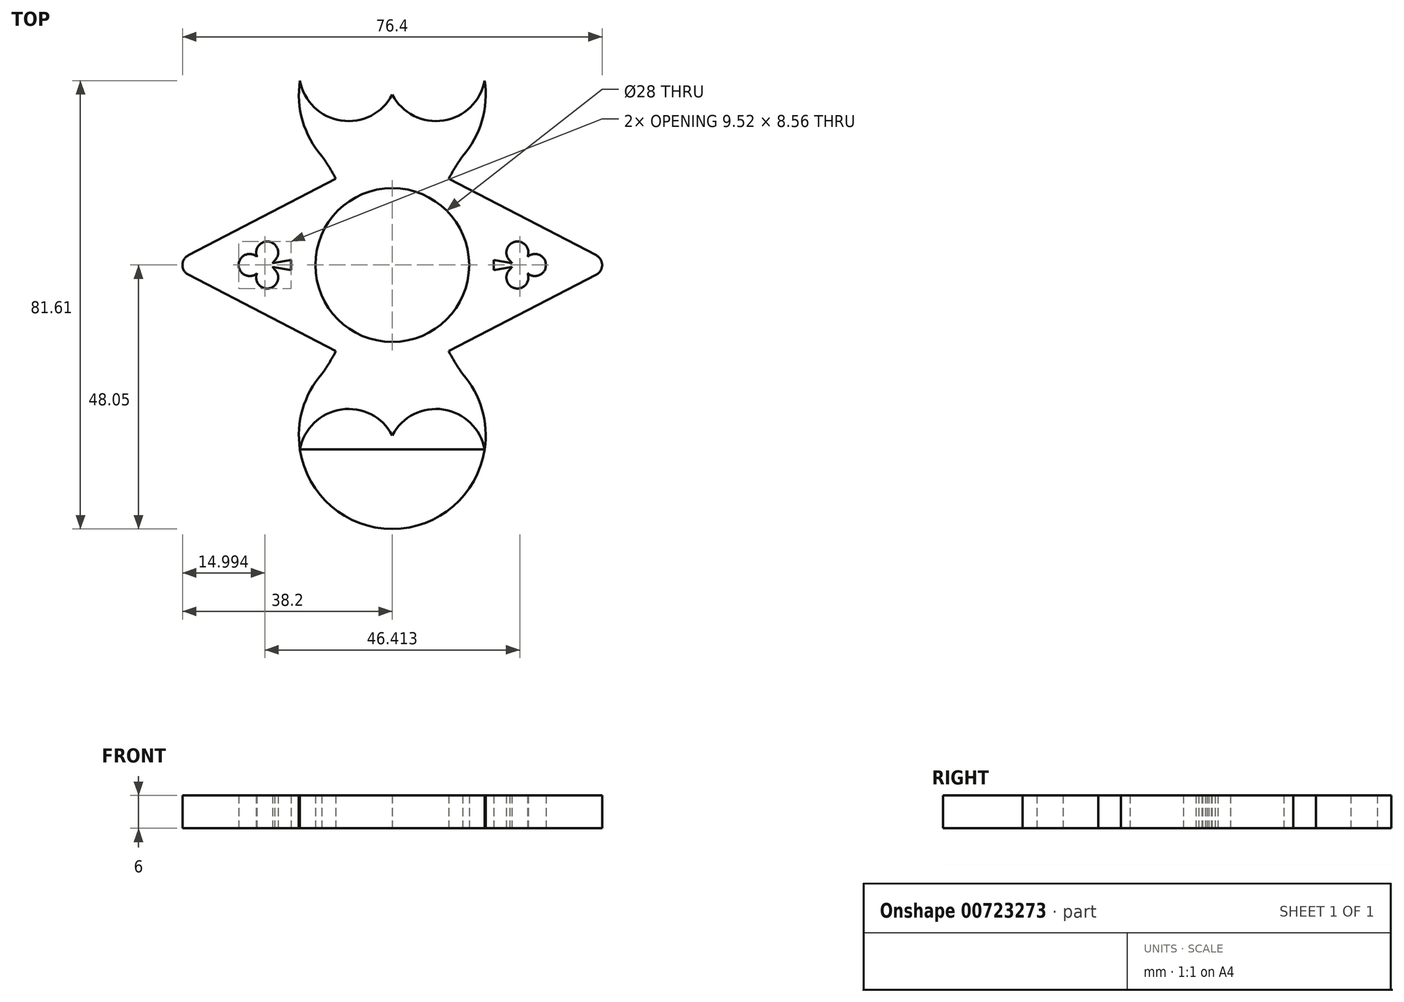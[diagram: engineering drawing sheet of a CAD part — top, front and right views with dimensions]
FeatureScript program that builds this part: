
annotation { "Feature Type Name" : "Feature", "Feature Type Description" : "" }
export const myFeature = defineFeature(function(context is Context, id is Id, definition is map)
    precondition{}
    {
        {
            var Q0;
            Q0=qCreatedBy(makeId("Top.planeOp"),FACE);
            var sketch = newSketch(context, id + "F0", { "sketchPlane" : qUnion([Q0])});
            skCircle(sketch, "E0", {"center": v(0, 0) * mm, "radius": 11 * mm});
            skCircle(sketch, "E1", {"center": v(0, 0) * mm, "radius": 14 * mm});
            skArc(sketch, "E2", {"start": v(-16.8, 33.56) * mm, "mid": v(0, 14) * mm, "end": v(16.8, 33.56) * mm});
            skArc(sketch, "E3", {"start": v(-16.8, 33.56) * mm, "mid": v(-9.31, 26.3) * mm, "end": v(0, 31) * mm});
            skArc(sketch, "E4", {"start": v(0, 31) * mm, "mid": v(9.31, 26.3) * mm, "end": v(16.8, 33.56) * mm});
            skArc(sketch, "E5.MirrorCS", {"start": v(-16.8, -33.56) * mm, "mid": v(-9.31, -26.3) * mm, "end": v(0, -31) * mm});
            skArc(sketch, "E6.MirrorCS", {"start": v(-16.8, -33.56) * mm, "mid": v(0, -14) * mm, "end": v(16.8, -33.56) * mm});
            skArc(sketch, "E7.MirrorCS", {"start": v(0, -31) * mm, "mid": v(9.31, -26.3) * mm, "end": v(16.8, -33.56) * mm});
            skArc(sketch, "E8", {"start": v(-12.8, -19.82) * mm, "mid": v(-11.47, -17.8) * mm, "end": v(-10.27, -15.68) * mm});
            skArc(sketch, "E9.trimOffspring", {"start": v(-10.27, 15.68) * mm, "mid": v(-11.47, 17.8) * mm, "end": v(-12.8, 19.82) * mm});
            skLineSegment(sketch, "E10", {"start": v(-10.27, 15.68) * mm, "end": v(-40.54, 0) * mm});
            skLineSegment(sketch, "E11", {"start": v(-10.27, -15.68) * mm, "end": v(-40.54, 0) * mm});
            skLineSegment(sketch, "E12.MirrorCS", {"start": v(-10.27, 15.68) * mm, "end": v(-37.12, 1.78) * mm});
            skLineSegment(sketch, "E13.MirrorCS", {"start": v(-10.27, -15.68) * mm, "end": v(-37.12, -1.78) * mm});
            skArc(sketch, "E14.MirrorCS", {"start": v(-10.27, -15.68) * mm, "mid": v(-11.47, -17.8) * mm, "end": v(-12.8, -19.82) * mm});
            skLineSegment(sketch, "E15.MirrorCS", {"start": v(10.27, 15.68) * mm, "end": v(37.12, 1.78) * mm});
            skLineSegment(sketch, "E16.MirrorCS", {"start": v(10.27, -15.68) * mm, "end": v(40.54, 0) * mm});
            skLineSegment(sketch, "E17.MirrorCS", {"start": v(10.27, -15.68) * mm, "end": v(37.12, -1.78) * mm});
            skLineSegment(sketch, "E18.MirrorCS", {"start": v(10.27, 15.68) * mm, "end": v(40.54, 0) * mm});
            skArc(sketch, "E19", {"start": v(-24.6, 1.45) * mm, "mid": v(-27.97, 0) * mm, "end": v(-24.6, -1.48) * mm});
            skArc(sketch, "E20", {"start": v(-21.41, 0.81) * mm, "mid": v(-22.39, 4.24) * mm, "end": v(-24.6, 1.45) * mm});
            skArc(sketch, "E21", {"start": v(-24.6, -1.48) * mm, "mid": v(-22.37, -4.24) * mm, "end": v(-21.41, -0.81) * mm});
            skPoint(sketch, "E22.orphan", {"position": v(-24.15, 0.81) * mm});
            skPoint(sketch, "E23.orphan", {"position": v(-24.14, -0.81) * mm});
            skLineSegment(sketch, "E24", {"start": v(-21.77, 0.33) * mm, "end": v(-18.44, 0.92) * mm});
            skLineSegment(sketch, "E25", {"start": v(-21.77, 0) * mm, "end": v(-16.49, 0) * mm, "construction": true});
            skLineSegment(sketch, "E26.MirrorCS", {"start": v(-21.77, -0.33) * mm, "end": v(-18.44, -0.92) * mm});
            skLineSegment(sketch, "E27", {"start": v(-18.44, -0.92) * mm, "end": v(-18.44, 0.92) * mm});
            skFitSpline(sketch, "E28", {"points": [v(-21.41, -0.81) * mm, v(-21.77, -0.33) * mm, v(-21.77, 0) * mm], "startDerivative": vector(-0.8, 0.89) * mm, "endDerivative": vector(0.13, 0.76) * mm});
            skFitSpline(sketch, "E29.MirrorCS", {"points": [v(-21.41, 0.81) * mm, v(-21.77, 0.33) * mm, v(-21.77, 0) * mm], "startDerivative": vector(-0.8, -0.89) * mm, "endDerivative": vector(0.13, -0.76) * mm});
            skFitSpline(sketch, "E30.MirrorCS", {"points": [v(-21.41, 0.81) * mm, v(-21.77, 0.33) * mm, v(-21.77, 0) * mm], "startDerivative": vector(-0.8, -0.89) * mm, "endDerivative": vector(0.13, -0.76) * mm});
            skFitSpline(sketch, "E31.MirrorCS", {"points": [v(-21.41, -0.81) * mm, v(-21.77, -0.33) * mm, v(-21.77, 0) * mm], "startDerivative": vector(-0.8, 0.89) * mm, "endDerivative": vector(0.13, 0.76) * mm});
            skPoint(sketch, "E32.MirrorP", {"position": v(-24.15, -0.81) * mm});
            skArc(sketch, "E33.MirrorCS", {"start": v(-24.6, -1.45) * mm, "mid": v(-27.97, 0) * mm, "end": v(-24.6, 1.48) * mm});
            skArc(sketch, "E34.MirrorCS", {"start": v(-21.41, -0.81) * mm, "mid": v(-22.39, -4.24) * mm, "end": v(-24.6, -1.45) * mm});
            skArc(sketch, "E35.MirrorCS", {"start": v(-24.6, 1.48) * mm, "mid": v(-22.37, 4.24) * mm, "end": v(-21.41, 0.81) * mm});
            skPoint(sketch, "E36.MirrorP", {"position": v(-24.14, 0.81) * mm});
            skLineSegment(sketch, "E37.MirrorCS", {"start": v(-18.44, 0.92) * mm, "end": v(-18.44, -0.92) * mm});
            skArc(sketch, "E38.MirrorCS", {"start": v(10.27, 15.68) * mm, "mid": v(11.47, 17.8) * mm, "end": v(12.8, 19.82) * mm});
            skFitSpline(sketch, "E39.MirrorCS", {"points": [v(21.41, -0.81) * mm, v(21.77, -0.33) * mm, v(21.77, 0) * mm], "startDerivative": vector(0.8, 0.89) * mm, "endDerivative": vector(-0.13, 0.76) * mm});
            skFitSpline(sketch, "E40.MirrorCS", {"points": [v(21.41, 0.81) * mm, v(21.77, 0.33) * mm, v(21.77, 0) * mm], "startDerivative": vector(0.8, -0.89) * mm, "endDerivative": vector(-0.13, -0.76) * mm});
            skPoint(sketch, "E41.MirrorP", {"position": v(24.15, 0.81) * mm});
            skPoint(sketch, "E42.MirrorP", {"position": v(24.15, -0.81) * mm});
            skLineSegment(sketch, "E43.MirrorCS", {"start": v(21.77, -0.33) * mm, "end": v(18.44, -0.92) * mm});
            skLineSegment(sketch, "E44.MirrorCS", {"start": v(21.77, 0.33) * mm, "end": v(18.44, 0.92) * mm});
            skLineSegment(sketch, "E45.MirrorCS", {"start": v(18.44, -0.92) * mm, "end": v(18.44, 0.92) * mm});
            skPoint(sketch, "E46.MirrorP", {"position": v(24.14, 0.81) * mm});
            skLineSegment(sketch, "E47.MirrorCS", {"start": v(21.77, 0) * mm, "end": v(16.49, 0) * mm, "construction": true});
            skArc(sketch, "E48.MirrorCS", {"start": v(24.6, 1.45) * mm, "mid": v(27.97, 0) * mm, "end": v(24.6, -1.48) * mm});
            skLineSegment(sketch, "E49.MirrorCS", {"start": v(18.44, 0.92) * mm, "end": v(18.44, -0.92) * mm});
            skPoint(sketch, "E50.MirrorP", {"position": v(24.14, -0.81) * mm});
            skArc(sketch, "E51.MirrorCS", {"start": v(21.41, 0.81) * mm, "mid": v(22.39, 4.24) * mm, "end": v(24.6, 1.45) * mm});
            skArc(sketch, "E52.MirrorCS", {"start": v(21.41, -0.81) * mm, "mid": v(22.39, -4.24) * mm, "end": v(24.6, -1.45) * mm});
            skArc(sketch, "E53.MirrorCS", {"start": v(24.6, -1.48) * mm, "mid": v(22.37, -4.24) * mm, "end": v(21.41, -0.81) * mm});
            skArc(sketch, "E54.MirrorCS", {"start": v(24.6, -1.45) * mm, "mid": v(27.97, 0) * mm, "end": v(24.6, 1.48) * mm});
            skArc(sketch, "E55.MirrorCS", {"start": v(24.6, 1.48) * mm, "mid": v(22.37, 4.24) * mm, "end": v(21.41, 0.81) * mm});
            skArc(sketch, "E56.MirrorCS", {"start": v(12.8, -19.82) * mm, "mid": v(11.47, -17.8) * mm, "end": v(10.27, -15.68) * mm});
            skArc(sketch, "E57.filletArc", {"start": v(37.12, -1.78) * mm, "mid": v(38.2, 0) * mm, "end": v(37.12, 1.78) * mm});
            skArc(sketch, "E58.filletArc", {"start": v(-37.12, 1.78) * mm, "mid": v(-38.2, 0) * mm, "end": v(-37.12, -1.78) * mm});
            skSolve(sketch);
        }
        {
            var Q0;
            Q0 = qSketchRegion(id + "F0", true);
            extrude(context, id + "F1", {"entities" : qUnion([Q0]), "depth" : 6 * mm, "offsetDistance" : 25 * mm});
        }
        {
            var Q0;
            Q0=makeQuery(id+"F1.opExtrude","SWEPT_EDGE",EDGE,{"disambiguationData":[OSD([sQuery(id+"F0.wireOp",EDGE,"E10"),sQuery(id+"F0.wireOp",EDGE,"E11")])]});
            var Q1;
            Q1=makeQuery(id+"F1.opExtrude","SWEPT_EDGE",EDGE,{"disambiguationData":[OSD([sQuery(id+"F0.wireOp",EDGE,"E16.MirrorCS"),sQuery(id+"F0.wireOp",EDGE,"E18.MirrorCS")])]});
            fillet(context, id + "F2", {"entities" : qUnion([Q0, Q1]), "radius" : 2 * mm, "tangentPropagation" : true, "allowEdgeOverflow" : false});
        }
        {
            var Q0;
            Q0=makeQuery(id+"F1.opExtrude","CAP_FACE",FACE,{"disambiguationData":[OSD([sQuery(id+"F0.wireOp",EDGE,"E1"),sQuery(id+"F0.wireOp",EDGE,"E2"),sQuery(id+"F0.wireOp",EDGE,"E3"),sQuery(id+"F0.wireOp",EDGE,"E4"),sQuery(id+"F0.wireOp",EDGE,"E5.MirrorCS"),sQuery(id+"F0.wireOp",EDGE,"E6.MirrorCS"),sQuery(id+"F0.wireOp",EDGE,"E7.MirrorCS"),sQuery(id+"F0.wireOp",EDGE,"E9.trimOffspring"),sQuery(id+"F0.wireOp",EDGE,"E14.MirrorCS"),sQuery(id+"F0.wireOp",EDGE,"E10"),sQuery(id+"F0.wireOp",EDGE,"E11"),sQuery(id+"F0.wireOp",EDGE,"E16.MirrorCS"),sQuery(id+"F0.wireOp",EDGE,"E18.MirrorCS"),sQuery(id+"F0.wireOp",EDGE,"E19"),sQuery(id+"F0.wireOp",EDGE,"E20"),sQuery(id+"F0.wireOp",EDGE,"E21"),sQuery(id+"F0.wireOp",EDGE,"E30.MirrorCS"),sQuery(id+"F0.wireOp",EDGE,"E31.MirrorCS"),sQuery(id+"F0.wireOp",EDGE,"E26.MirrorCS"),sQuery(id+"F0.wireOp",EDGE,"E33.MirrorCS"),sQuery(id+"F0.wireOp",EDGE,"E34.MirrorCS"),sQuery(id+"F0.wireOp",EDGE,"E35.MirrorCS"),sQuery(id+"F0.wireOp",EDGE,"E24"),sQuery(id+"F0.wireOp",EDGE,"E37.MirrorCS"),sQuery(id+"F0.wireOp",EDGE,"E38.MirrorCS"),sQuery(id+"F0.wireOp",EDGE,"E39.MirrorCS"),sQuery(id+"F0.wireOp",EDGE,"E40.MirrorCS"),sQuery(id+"F0.wireOp",EDGE,"E44.MirrorCS"),sQuery(id+"F0.wireOp",EDGE,"E48.MirrorCS"),sQuery(id+"F0.wireOp",EDGE,"E49.MirrorCS"),sQuery(id+"F0.wireOp",EDGE,"E51.MirrorCS"),sQuery(id+"F0.wireOp",EDGE,"E52.MirrorCS"),sQuery(id+"F0.wireOp",EDGE,"E43.MirrorCS"),sQuery(id+"F0.wireOp",EDGE,"E53.MirrorCS"),sQuery(id+"F0.wireOp",EDGE,"E54.MirrorCS"),sQuery(id+"F0.wireOp",EDGE,"E55.MirrorCS"),sQuery(id+"F0.wireOp",EDGE,"E56.MirrorCS")])],"isStart":true});
            var sketch = newSketch(context, id + "F3", { "sketchPlane" : qUnion([Q0])});
            skLineSegment(sketch, "E59", {"start": v(-16.8, 33.56) * mm, "end": v(16.8, 33.56) * mm});
            skArc(sketch, "E60", {"start": v(16.8, 33.56) * mm, "mid": v(0, 48.05) * mm, "end": v(-16.8, 33.56) * mm});
            skSolve(sketch);
        }
        {
            var Q0;
            Q0=makeQuery(id+"F3.imprint","IMPRINT",FACE,{"disambiguationData":[TD([[makeQuery(id+"F3.imprint","IMPRINT",EDGE,{"derivedFrom":sQuery(id+"F3.wireOp",EDGE,"E59")}),1.0]])]});
            extrude(context, id + "F4", {"entities" : qUnion([Q0]), "oppositeDirection" : true, "depth" : 6 * mm, "offsetDistance" : 25 * mm});
        }
    });
